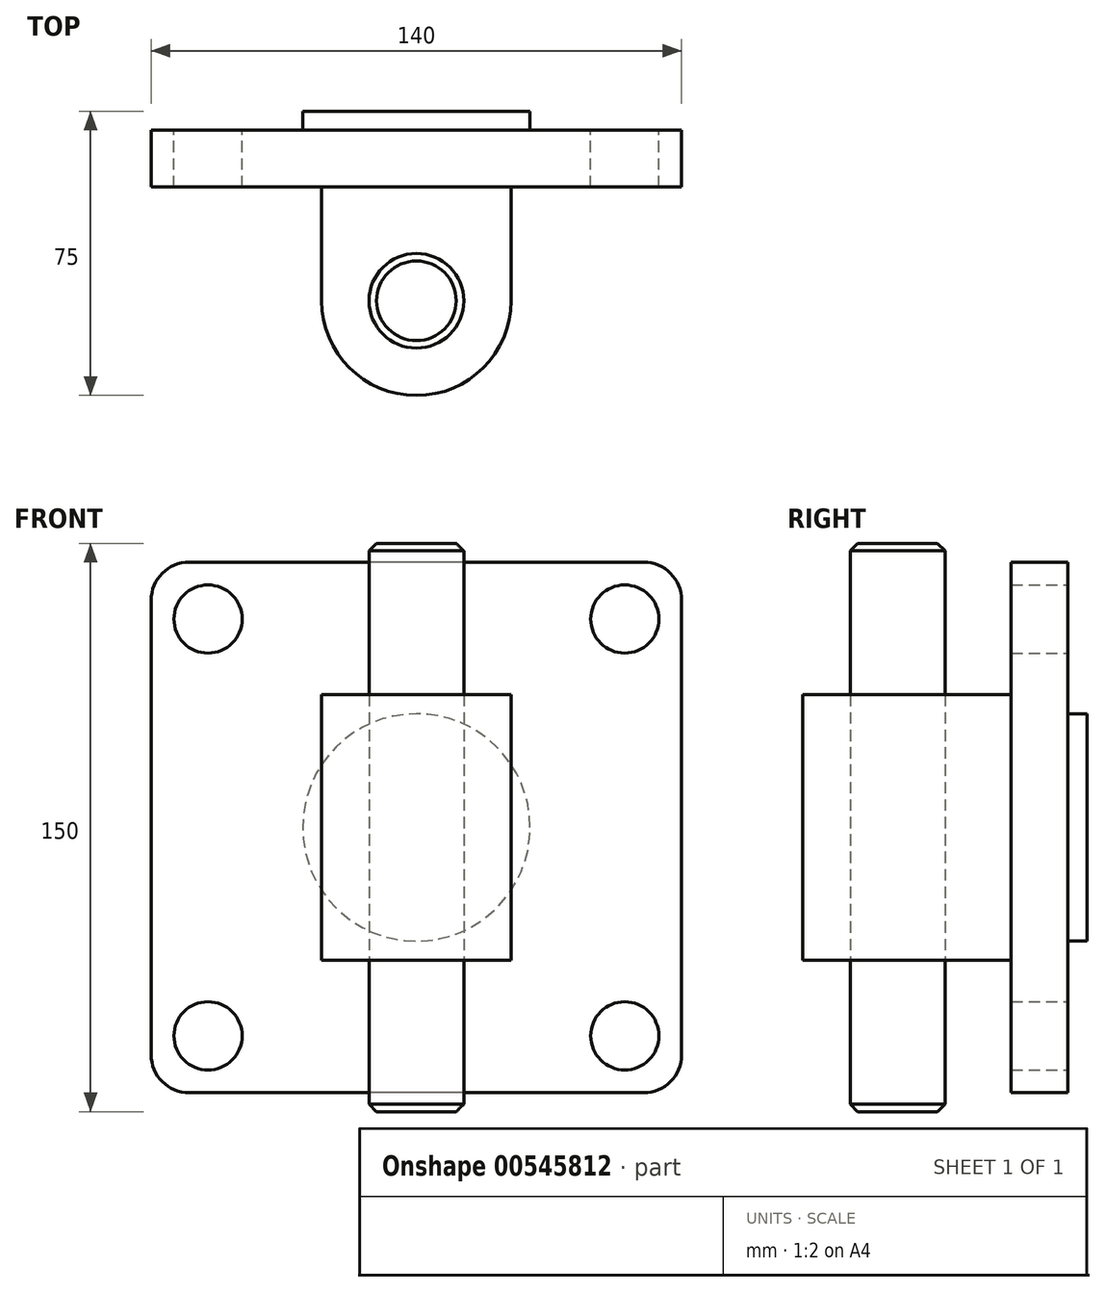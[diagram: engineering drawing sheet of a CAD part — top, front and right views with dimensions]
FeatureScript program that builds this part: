
annotation { "Feature Type Name" : "Feature", "Feature Type Description" : "" }
export const myFeature = defineFeature(function(context is Context, id is Id, definition is map)
    precondition{}
    {
        {
            var Q0;
            Q0=qCreatedBy(makeId("Front.planeOp"),FACE);
            var sketch = newSketch(context, id + "F0", { "sketchPlane" : qUnion([Q0])});
            skLineSegment(sketch, "E0.bottom", {"start": v(60, -70) * mm, "end": v(-60, -70) * mm});
            skLineSegment(sketch, "E0.top", {"start": v(60, 70) * mm, "end": v(-60, 70) * mm});
            skLineSegment(sketch, "E0.left", {"start": v(70, -60) * mm, "end": v(70, 60) * mm});
            skLineSegment(sketch, "E0.right", {"start": v(-70, -60) * mm, "end": v(-70, 60) * mm});
            skPoint(sketch, "E0.middle", {"position": v(0, 0) * mm});
            skPoint(sketch, "E1.visualSharp", {"position": v(-70, 70) * mm});
            skArc(sketch, "E1.filletArc", {"start": v(-60, 70) * mm, "mid": v(-67.07, 67.07) * mm, "end": v(-70, 60) * mm});
            skPoint(sketch, "E2.visualSharp", {"position": v(70, 70) * mm});
            skArc(sketch, "E2.filletArc", {"start": v(70, 60) * mm, "mid": v(67.07, 67.07) * mm, "end": v(60, 70) * mm});
            skPoint(sketch, "E3.visualSharp", {"position": v(70, -70) * mm});
            skArc(sketch, "E3.filletArc", {"start": v(60, -70) * mm, "mid": v(67.07, -67.07) * mm, "end": v(70, -60) * mm});
            skPoint(sketch, "E4.visualSharp", {"position": v(-70, -70) * mm});
            skArc(sketch, "E4.filletArc", {"start": v(-70, -60) * mm, "mid": v(-67.07, -67.07) * mm, "end": v(-60, -70) * mm});
            skLineSegment(sketch, "E5", {"start": v(0, 70) * mm, "end": v(0, -70) * mm, "construction": true});
            skLineSegment(sketch, "E6.0", {"start": v(-55, 47.5) * mm, "end": v(-55, -47.5) * mm, "construction": true});
            skLineSegment(sketch, "E7.0", {"start": v(55, 47.5) * mm, "end": v(55, -47.5) * mm, "construction": true});
            skLineSegment(sketch, "E8", {"start": v(-70, 0) * mm, "end": v(70, 0) * mm, "construction": true});
            skLineSegment(sketch, "E9.0", {"start": v(-47.5, -55) * mm, "end": v(47.5, -55) * mm, "construction": true});
            skLineSegment(sketch, "E10.0", {"start": v(-47.5, 55) * mm, "end": v(47.5, 55) * mm, "construction": true});
            skCircle(sketch, "E11", {"center": v(-55, 55) * mm, "radius": 9 * mm});
            skCircle(sketch, "E12", {"center": v(55, 55) * mm, "radius": 9 * mm});
            skCircle(sketch, "E13", {"center": v(-55, -55) * mm, "radius": 9 * mm});
            skCircle(sketch, "E14", {"center": v(55, -55) * mm, "radius": 9 * mm});
            skSolve(sketch);
        }
        {
            var Q0;
            Q0=makeQuery(id+"F0.imprint","IMPRINT",FACE,{"disambiguationData":[TD([[makeQuery(id+"F0.imprint","IMPRINT",EDGE,{"derivedFrom":sQuery(id+"F0.wireOp",EDGE,"E0.bottom")}),-1.0]])]});
            extrude(context, id + "F1", {"entities" : qUnion([Q0]), "endBound" : BoundingType.SYMMETRIC, "depth" : 20 * mm, "offsetDistance" : 25 * mm});
        }
        {
            var Q0;
            Q0=makeQuery(id+"F1.opExtrude","CAP_FACE",FACE,{"disambiguationData":[OSD([sQuery(id+"F0.wireOp",EDGE,"E0.bottom"),sQuery(id+"F0.wireOp",EDGE,"E0.top"),sQuery(id+"F0.wireOp",EDGE,"E0.left"),sQuery(id+"F0.wireOp",EDGE,"E0.right"),sQuery(id+"F0.wireOp",EDGE,"E1.filletArc"),sQuery(id+"F0.wireOp",EDGE,"E2.filletArc"),sQuery(id+"F0.wireOp",EDGE,"E3.filletArc"),sQuery(id+"F0.wireOp",EDGE,"E4.filletArc"),sQuery(id+"F0.wireOp",EDGE,"E11"),sQuery(id+"F0.wireOp",EDGE,"E12"),sQuery(id+"F0.wireOp",EDGE,"E13"),sQuery(id+"F0.wireOp",EDGE,"E14")])],"isStart":false});
            var sketch = newSketch(context, id + "F2", { "sketchPlane" : qUnion([Q0])});
            skCircle(sketch, "E15", {"center": v(0, 0) * mm, "radius": 30 * mm});
            skSolve(sketch);
        }
        {
            var Q0;
            Q0=qCreatedBy(makeId("Top.planeOp"),FACE);
            var sketch = newSketch(context, id + "F3", { "sketchPlane" : qUnion([Q0])});
            skLineSegment(sketch, "E16", {"start": v(62.06, -40) * mm, "end": v(-61.89, -40) * mm, "construction": true});
            skLineSegment(sketch, "E17", {"start": v(0, 0) * mm, "end": v(0, -54.12) * mm, "construction": true});
            skArc(sketch, "E18", {"start": v(-25, -40) * mm, "mid": v(0, -65) * mm, "end": v(25, -40) * mm});
            skCircle(sketch, "E19", {"center": v(0, -40) * mm, "radius": 12.5 * mm});
            skLineSegment(sketch, "E20.0", {"start": v(30, -10) * mm, "end": v(-30, -10) * mm});
            skLineSegment(sketch, "E21", {"start": v(25, -40) * mm, "end": v(25, -10) * mm});
            skLineSegment(sketch, "E22", {"start": v(-25, -40) * mm, "end": v(-25, -10) * mm});
            skSolve(sketch);
        }
        {
            var Q0;
            Q0=qSketchRegion(id+"F3",true);
            extrude(context, id + "F4", {"entities" : qUnion([Q0]), "operationType" : NewBodyOperationType.ADD, "endBound" : BoundingType.SYMMETRIC, "depth" : 70 * mm, "offsetDistance" : 25 * mm});
        }
        {
            var Q0;
            Q0=makeQuery(id+"F1.opExtrude","CAP_FACE",FACE,{"disambiguationData":[OSD([sQuery(id+"F0.wireOp",EDGE,"E0.bottom"),sQuery(id+"F0.wireOp",EDGE,"E0.top"),sQuery(id+"F0.wireOp",EDGE,"E0.left"),sQuery(id+"F0.wireOp",EDGE,"E0.right"),sQuery(id+"F0.wireOp",EDGE,"E1.filletArc"),sQuery(id+"F0.wireOp",EDGE,"E2.filletArc"),sQuery(id+"F0.wireOp",EDGE,"E3.filletArc"),sQuery(id+"F0.wireOp",EDGE,"E4.filletArc"),sQuery(id+"F0.wireOp",EDGE,"E11"),sQuery(id+"F0.wireOp",EDGE,"E12"),sQuery(id+"F0.wireOp",EDGE,"E13"),sQuery(id+"F0.wireOp",EDGE,"E14")])],"isStart":true});
            var sketch = newSketch(context, id + "F5", { "sketchPlane" : qUnion([Q0])});
            skCircle(sketch, "E23.0", {"center": v(0, 0) * mm, "radius": 30 * mm});
            skSolve(sketch);
        }
        {
            var Q0;
            Q0=makeQuery(id+"F5.imprint","IMPRINT",FACE,{"disambiguationData":[TD([[makeQuery(id+"F5.imprint","IMPRINT",EDGE,{"derivedFrom":sQuery(id+"F5.wireOp",EDGE,"E23.0")}),-1.0]])]});
            extrude(context, id + "F6", {"entities" : qUnion([Q0]), "operationType" : NewBodyOperationType.REMOVE, "oppositeDirection" : true, "depth" : 5 * mm, "offsetDistance" : 25 * mm});
        }
        {
            var Q0;
            Q0=makeQuery(id+"F3.imprint","IMPRINT",FACE,{"disambiguationData":[TD([[makeQuery(id+"F3.imprint","IMPRINT",EDGE,{"derivedFrom":sQuery(id+"F3.wireOp",EDGE,"E19")}),1.0]])]});
            extrude(context, id + "F7", {"entities" : qUnion([Q0]), "endBound" : BoundingType.SYMMETRIC, "depth" : 150 * mm, "offsetDistance" : 25 * mm});
        }
        {
            var Q0;
            Q0=makeQuery(id+"F7.opExtrude","CAP_EDGE",EDGE,{"disambiguationData":[OSD([sQuery(id+"F3.wireOp",EDGE,"E19")])],"isStart":false});
            var Q1;
            Q1=makeQuery(id+"F7.opExtrude","CAP_EDGE",EDGE,{"disambiguationData":[OSD([sQuery(id+"F3.wireOp",EDGE,"E19")])],"isStart":true});
            chamfer(context, id + "F8", {"entities" : qUnion([Q0, Q1]), "width" : 2 * mm, "tangentPropagation" : true});
        }
    });
